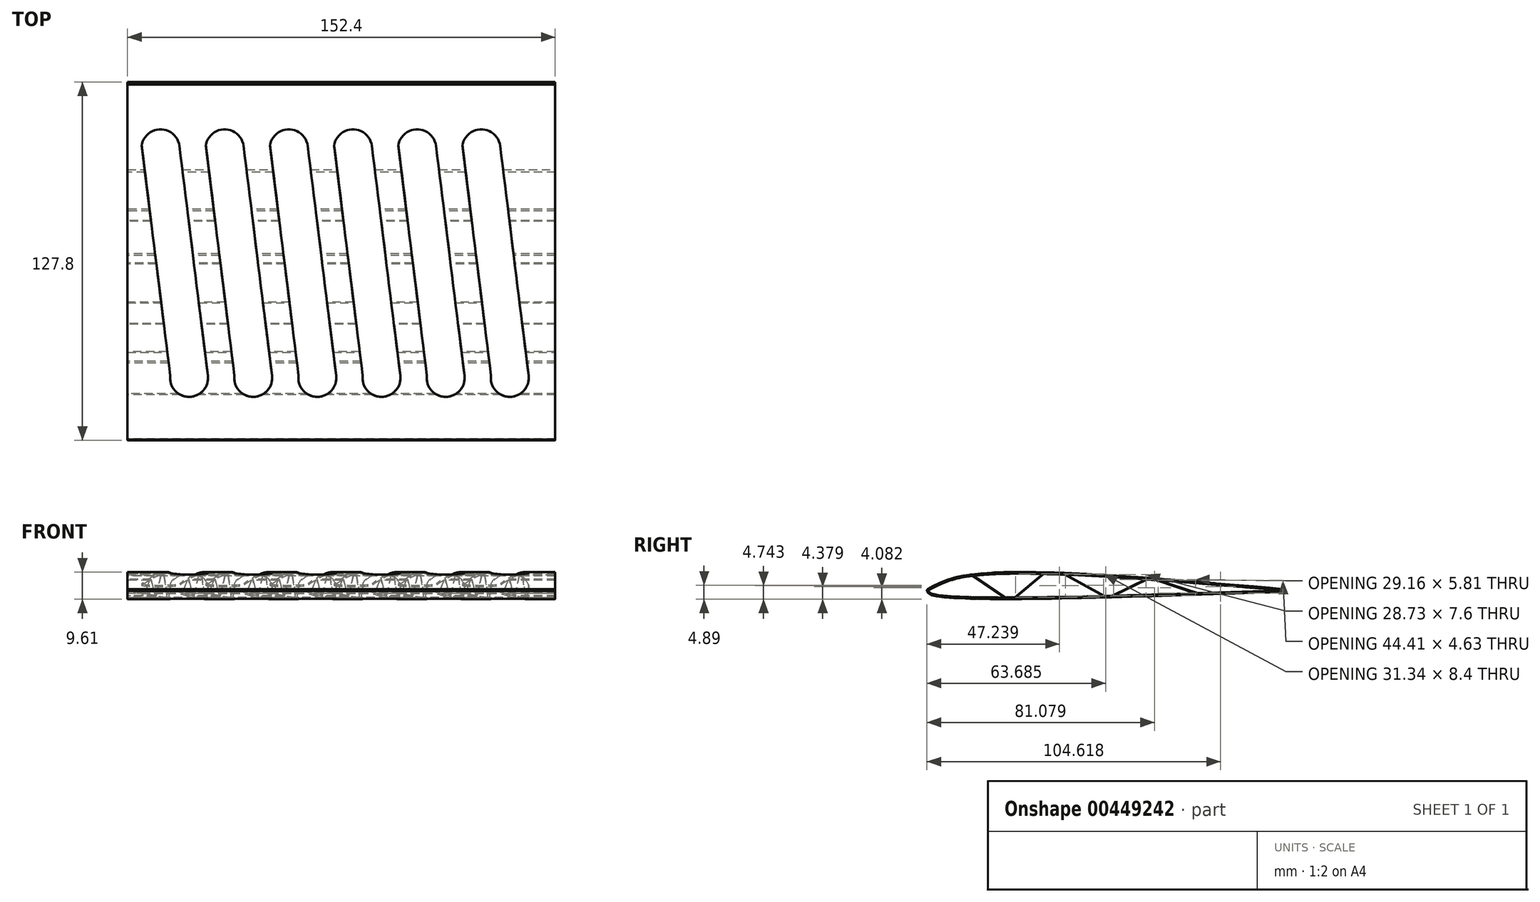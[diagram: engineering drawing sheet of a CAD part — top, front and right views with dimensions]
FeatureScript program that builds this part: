
annotation { "Feature Type Name" : "Feature", "Feature Type Description" : "" }
export const myFeature = defineFeature(function(context is Context, id is Id, definition is map)
    precondition{}
    {
        {
            var Q0;
            Q0=qCreatedBy(makeId("Right.planeOp"),FACE);
            var sketch = newSketch(context, id + "F0", { "sketchPlane" : qUnion([Q0])});
            skFitSpline(sketch, "E0", {"points": [v(-58.71, 0) * mm, v(-44.42, 5) * mm, v(67.61, 0) * mm], "startDerivative": vector(39.76, 22.05) * mm, "endDerivative": vector(189.77, -16.16) * mm});
            skFitSpline(sketch, "E1", {"points": [v(-58.71, 0) * mm, v(-57.76, -1.05) * mm, v(67.61, 0) * mm], "startDerivative": vector(3.72, -11.52) * mm, "endDerivative": vector(196.93, 6.64) * mm});
            skFitSpline(sketch, "E2.0", {"points": [v(-58.96, 0.44) * mm, v(-58.13, 0.9) * mm, v(-56.47, 1.83) * mm, v(-53.67, 3.16) * mm, v(-50.87, 4.15) * mm, v(-48.22, 4.83) * mm, v(-46, 5.28) * mm, v(-43.5, 5.66) * mm, v(-39.8, 6.07) * mm, v(-34.48, 6.4) * mm, v(-27.11, 6.54) * mm, v(-16.09, 6.41) * mm, v(-0.32, 5.75) * mm, v(21.01, 4.34) * mm, v(43.94, 2.53) * mm, v(59.75, 1.18) * mm, v(67.66, 0.5) * mm]});
            skFitSpline(sketch, "E3.0", {"points": [v(-59.2, -0.16) * mm, v(-59.16, -0.28) * mm, v(-59.09, -0.5) * mm, v(-58.9, -0.83) * mm, v(-58.6, -1.16) * mm, v(-58.08, -1.5) * mm, v(-57.14, -1.82) * mm, v(-55.88, -2.08) * mm, v(-53.75, -2.38) * mm, v(-50.26, -2.68) * mm, v(-44.82, -2.91) * mm, v(-38.25, -3.04) * mm, v(-30.63, -3.06) * mm, v(-19.22, -2.98) * mm, v(-2.88, -2.68) * mm, v(19.23, -2.09) * mm, v(43.02, -1.34) * mm, v(59.43, -0.78) * mm, v(67.63, -0.5) * mm]});
            skArc(sketch, "E4", {"start": v(-58.96, 0.44) * mm, "mid": v(-59.16, 0.18) * mm, "end": v(-59.2, -0.16) * mm});
            skArc(sketch, "E5", {"start": v(67.63, -0.5) * mm, "mid": v(68.6, -0.03) * mm, "end": v(67.66, 0.5) * mm});
            skSolve(sketch);
        }
        {
            var Q0;
            Q0 = qSketchRegion(id + "F0", true);
            extrude(context, id + "F1", {"entities" : qUnion([Q0]), "depth" : 152.4 * mm});
        }
        {
            var Q0;
            Q0=makeQuery(id+"F1.opExtrude","CAP_FACE",FACE,{"disambiguationData":[OSD([sQuery(id+"F0.wireOp",EDGE,"E0"),sQuery(id+"F0.wireOp",EDGE,"E1"),sQuery(id+"F0.wireOp",EDGE,"E2.0"),sQuery(id+"F0.wireOp",EDGE,"E3.0"),sQuery(id+"F0.wireOp",EDGE,"E4"),sQuery(id+"F0.wireOp",EDGE,"E5")])],"isStart":false});
            var sketch = newSketch(context, id + "F2", { "sketchPlane" : qUnion([Q0])});
            skLineSegment(sketch, "E6", {"start": v(-43.3, 5.42) * mm, "end": v(-31.5, -2.62) * mm});
            skLineSegment(sketch, "E7", {"start": v(-31.5, -2.62) * mm, "end": v(-30.9, -2.62) * mm});
            skLineSegment(sketch, "E8", {"start": v(-30.9, -2.62) * mm, "end": v(-42.88, 5.47) * mm});
            skLineSegment(sketch, "E9", {"start": v(-42.88, 5.47) * mm, "end": v(-43.3, 5.42) * mm});
            skSolve(sketch);
        }
        {
            var Q0;
            Q0 = qSketchRegion(id + "F2", true);
            extrude(context, id + "F3", {"entities" : qUnion([Q0]), "operationType" : NewBodyOperationType.ADD, "oppositeDirection" : true, "depth" : 152.4 * mm});
        }
        {
            var Q0;
            Q0=makeQuery(id+"F3.boolean.opBoolean","MERGE",FACE,{"derivedFrom":[makeQuery(id+"F1.opExtrude","CAP_FACE",FACE,{"disambiguationData":[OSD([sQuery(id+"F0.wireOp",EDGE,"E0"),sQuery(id+"F0.wireOp",EDGE,"E1"),sQuery(id+"F0.wireOp",EDGE,"E2.0"),sQuery(id+"F0.wireOp",EDGE,"E3.0"),sQuery(id+"F0.wireOp",EDGE,"E4"),sQuery(id+"F0.wireOp",EDGE,"E5")])],"isStart":false}),makeQuery(id+"F3.opExtrude","CAP_FACE",FACE,{"disambiguationData":[OSD([sQuery(id+"F2.wireOp",EDGE,"E6"),sQuery(id+"F2.wireOp",EDGE,"E7"),sQuery(id+"F2.wireOp",EDGE,"E8"),sQuery(id+"F2.wireOp",EDGE,"E9")])],"isStart":true})]});
            var sketch = newSketch(context, id + "F4", { "sketchPlane" : qUnion([Q0])});
            skLineSegment(sketch, "E10", {"start": v(-10.15, 5.63) * mm, "end": v(3.7, -2) * mm});
            skLineSegment(sketch, "E11", {"start": v(3.7, -2) * mm, "end": v(4, -2) * mm});
            skLineSegment(sketch, "E12", {"start": v(4, -2) * mm, "end": v(-9.96, 5.66) * mm});
            skLineSegment(sketch, "E13", {"start": v(-9.96, 5.66) * mm, "end": v(-10.15, 5.63) * mm});
            skLineSegment(sketch, "E14", {"start": v(-27.9, -2.59) * mm, "end": v(-17.75, 5.98) * mm});
            skLineSegment(sketch, "E15", {"start": v(-17.75, 5.98) * mm, "end": v(-17.43, 5.98) * mm});
            skLineSegment(sketch, "E16", {"start": v(-17.43, 5.98) * mm, "end": v(-27.72, -2.6) * mm});
            skLineSegment(sketch, "E17", {"start": v(-27.72, -2.6) * mm, "end": v(-27.9, -2.59) * mm});
            skSolve(sketch);
        }
        {
            var Q0;
            Q0 = qSketchRegion(id + "F4", true);
            extrude(context, id + "F5", {"entities" : qUnion([Q0]), "operationType" : NewBodyOperationType.ADD, "oppositeDirection" : true, "depth" : 152.4 * mm});
        }
        {
            var Q0;
            Q0=makeQuery(id+"F5.boolean.opBoolean","MERGE",FACE,{"derivedFrom":[makeQuery(id+"F3.boolean.opBoolean","MERGE",FACE,{"derivedFrom":[makeQuery(id+"F1.opExtrude","CAP_FACE",FACE,{"disambiguationData":[OSD([sQuery(id+"F0.wireOp",EDGE,"E0"),sQuery(id+"F0.wireOp",EDGE,"E1"),sQuery(id+"F0.wireOp",EDGE,"E2.0"),sQuery(id+"F0.wireOp",EDGE,"E3.0"),sQuery(id+"F0.wireOp",EDGE,"E4"),sQuery(id+"F0.wireOp",EDGE,"E5")])],"isStart":false}),makeQuery(id+"F3.opExtrude","CAP_FACE",FACE,{"disambiguationData":[OSD([sQuery(id+"F2.wireOp",EDGE,"E6"),sQuery(id+"F2.wireOp",EDGE,"E7"),sQuery(id+"F2.wireOp",EDGE,"E8"),sQuery(id+"F2.wireOp",EDGE,"E9")])],"isStart":true})]}),makeQuery(id+"F5.opExtrude","CAP_FACE",FACE,{"disambiguationData":[OSD([sQuery(id+"F4.wireOp",EDGE,"E10"),sQuery(id+"F4.wireOp",EDGE,"E11"),sQuery(id+"F4.wireOp",EDGE,"E12"),sQuery(id+"F4.wireOp",EDGE,"E13")])],"isStart":true}),makeQuery(id+"F5.opExtrude","CAP_FACE",FACE,{"disambiguationData":[OSD([sQuery(id+"F4.wireOp",EDGE,"E14"),sQuery(id+"F4.wireOp",EDGE,"E15"),sQuery(id+"F4.wireOp",EDGE,"E16"),sQuery(id+"F4.wireOp",EDGE,"E17")])],"isStart":true})]});
            var sketch = newSketch(context, id + "F6", { "sketchPlane" : qUnion([Q0])});
            skLineSegment(sketch, "E18", {"start": v(6.3, -2.1) * mm, "end": v(19.09, 4.06) * mm});
            skLineSegment(sketch, "E19", {"start": v(19.09, 4.06) * mm, "end": v(19.44, 4.06) * mm});
            skLineSegment(sketch, "E20", {"start": v(19.44, 4.06) * mm, "end": v(6.8, -2.14) * mm});
            skLineSegment(sketch, "E21", {"start": v(6.8, -2.14) * mm, "end": v(6.3, -2.1) * mm});
            skLineSegment(sketch, "E22", {"start": v(22.12, 3.84) * mm, "end": v(36.9, -1.19) * mm});
            skLineSegment(sketch, "E23", {"start": v(36.9, -1.19) * mm, "end": v(37.27, -1) * mm});
            skLineSegment(sketch, "E24", {"start": v(37.27, -1) * mm, "end": v(22.56, 3.84) * mm});
            skLineSegment(sketch, "E25", {"start": v(22.56, 3.84) * mm, "end": v(22.12, 3.84) * mm});
            skSolve(sketch);
        }
        {
            var Q0;
            Q0 = qSketchRegion(id + "F6", true);
            extrude(context, id + "F7", {"entities" : qUnion([Q0]), "operationType" : NewBodyOperationType.ADD, "oppositeDirection" : true, "depth" : 152.4 * mm});
        }
        {
            var Q0;
            Q0=qCreatedBy(makeId("Top.planeOp"),FACE);
            var sketch = newSketch(context, id + "F8", { "sketchPlane" : qUnion([Q0])});
            skLineSegment(sketch, "E26", {"start": v(5.08, 45.76) * mm, "end": v(15.24, -36.12) * mm});
            skLineSegment(sketch, "E27", {"start": v(18.5, 45.76) * mm, "end": v(28.65, -36.12) * mm});
            skArc(sketch, "E28", {"start": v(18.5, 45.76) * mm, "mid": v(11.79, 51.68) * mm, "end": v(5.08, 45.76) * mm});
            skArc(sketch, "E29", {"start": v(15.24, -36.12) * mm, "mid": v(21.95, -43.71) * mm, "end": v(28.65, -36.12) * mm});
            skLineSegment(sketch, "E30.1.0.0", {"start": v(41.35, 45.76) * mm, "end": v(51.51, -36.12) * mm});
            skArc(sketch, "E30.1.0.1", {"start": v(41.35, 45.76) * mm, "mid": v(34.65, 51.68) * mm, "end": v(27.94, 45.76) * mm});
            skLineSegment(sketch, "E30.1.0.2", {"start": v(27.94, 45.76) * mm, "end": v(38.1, -36.12) * mm});
            skArc(sketch, "E30.1.0.3", {"start": v(38.1, -36.12) * mm, "mid": v(44.8, -43.71) * mm, "end": v(51.51, -36.12) * mm});
            skLineSegment(sketch, "E30.2.0.0", {"start": v(64.21, 45.76) * mm, "end": v(74.37, -36.12) * mm});
            skArc(sketch, "E30.2.0.1", {"start": v(64.21, 45.76) * mm, "mid": v(57.5, 51.68) * mm, "end": v(50.8, 45.76) * mm});
            skLineSegment(sketch, "E30.2.0.2", {"start": v(50.8, 45.76) * mm, "end": v(60.96, -36.12) * mm});
            skArc(sketch, "E30.2.0.3", {"start": v(60.96, -36.12) * mm, "mid": v(67.67, -43.71) * mm, "end": v(74.37, -36.12) * mm});
            skLineSegment(sketch, "E30.3.0.0", {"start": v(87.07, 45.76) * mm, "end": v(97.23, -36.12) * mm});
            skArc(sketch, "E30.3.0.1", {"start": v(87.07, 45.76) * mm, "mid": v(80.37, 51.68) * mm, "end": v(73.66, 45.76) * mm});
            skLineSegment(sketch, "E30.3.0.2", {"start": v(73.66, 45.76) * mm, "end": v(83.82, -36.12) * mm});
            skArc(sketch, "E30.3.0.3", {"start": v(83.82, -36.12) * mm, "mid": v(90.53, -43.71) * mm, "end": v(97.23, -36.12) * mm});
            skLineSegment(sketch, "E30.4.0.0", {"start": v(109.93, 45.76) * mm, "end": v(120.1, -36.12) * mm});
            skArc(sketch, "E30.4.0.1", {"start": v(109.93, 45.76) * mm, "mid": v(103.23, 51.68) * mm, "end": v(96.52, 45.76) * mm});
            skLineSegment(sketch, "E30.4.0.2", {"start": v(96.52, 45.76) * mm, "end": v(106.68, -36.12) * mm});
            skArc(sketch, "E30.4.0.3", {"start": v(106.68, -36.12) * mm, "mid": v(113.39, -43.71) * mm, "end": v(120.1, -36.12) * mm});
            skLineSegment(sketch, "E30.5.0.0", {"start": v(132.8, 45.76) * mm, "end": v(142.95, -36.12) * mm});
            skArc(sketch, "E30.5.0.1", {"start": v(132.8, 45.76) * mm, "mid": v(126.09, 51.68) * mm, "end": v(119.38, 45.76) * mm});
            skLineSegment(sketch, "E30.5.0.2", {"start": v(119.38, 45.76) * mm, "end": v(129.54, -36.12) * mm});
            skArc(sketch, "E30.5.0.3", {"start": v(129.54, -36.12) * mm, "mid": v(136.25, -43.71) * mm, "end": v(142.95, -36.12) * mm});
            skLineSegment(sketch, "E30.direction1", {"start": v(28.65, -36.12) * mm, "end": v(51.51, -36.12) * mm, "construction": true});
            skSolve(sketch);
        }
        {
            var Q0;
            Q0 = qSketchRegion(id + "F8", true);
            extrude(context, id + "F9", {"entities" : qUnion([Q0]), "operationType" : NewBodyOperationType.REMOVE, "depth" : 25.4 * mm, "hasSecondDirection" : true, "secondDirectionOppositeDirection" : true, "secondDirectionDepth" : 25.4 * mm});
        }
    });
